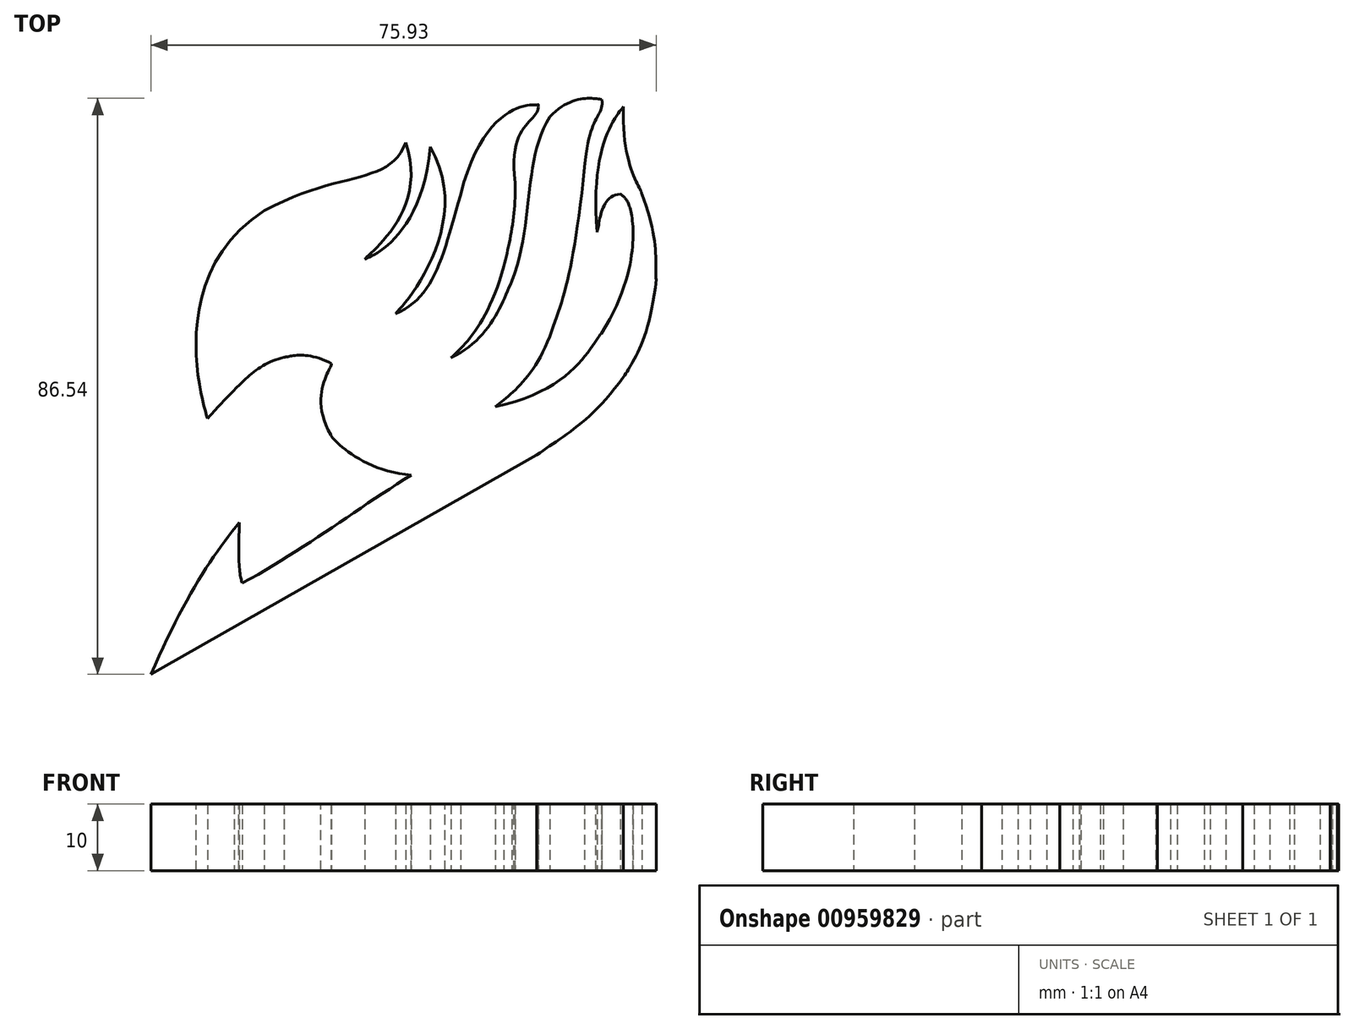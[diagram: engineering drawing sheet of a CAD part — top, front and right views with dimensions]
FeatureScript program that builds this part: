
annotation { "Feature Type Name" : "Feature", "Feature Type Description" : "" }
export const myFeature = defineFeature(function(context is Context, id is Id, definition is map)
    precondition{}
    {
        {
            var Q0;
            Q0=qCreatedBy(makeId("Top.planeOp"),FACE);
            var sketch = newSketch(context, id + "F0", { "sketchPlane" : qUnion([Q0])});
            skFitSpline(sketch, "E0", {"points": [v(8.52, 38.4) * mm, v(17.05, 69.64) * mm], "startDerivative": vector(-0.44, 1.4) * mm, "endDerivative": vector(47.56, 30.17) * mm});
            skFitSpline(sketch, "E1", {"points": [v(17.05, 69.64) * mm, v(38.3, 79.88) * mm], "startDerivative": vector(34.34, 18.82) * mm, "endDerivative": vector(7.6, 19.81) * mm});
            skFitSpline(sketch, "E2", {"points": [v(38.3, 79.88) * mm, v(32.13, 62.27) * mm], "startDerivative": vector(10.9, -31.7) * mm, "endDerivative": vector(0, -1.98) * mm});
            skFitSpline(sketch, "E3", {"points": [v(32.13, 62.27) * mm, v(41.98, 79.22) * mm], "startDerivative": vector(-2.8, 0) * mm, "endDerivative": vector(4.05, 45.39) * mm});
            skFitSpline(sketch, "E4", {"points": [v(41.98, 79.22) * mm, v(36.55, 54.12) * mm], "startDerivative": vector(22.19, -37.86) * mm, "endDerivative": vector(2.45, 4.02) * mm});
            skFitSpline(sketch, "E5", {"points": [v(36.55, 54.12) * mm, v(46.52, 72.02) * mm], "startDerivative": vector(17.84, 6.65) * mm, "endDerivative": vector(8.05, 28.34) * mm});
            skFitSpline(sketch, "E6", {"points": [v(46.52, 72.02) * mm, v(58.18, 85.6) * mm], "startDerivative": vector(12.25, 47.76) * mm, "endDerivative": vector(-2.45, 1.22) * mm});
            skFitSpline(sketch, "E7", {"points": [v(54.72, 73.88) * mm, v(53.05, 61.3) * mm], "startDerivative": vector(0.6, -12.92) * mm, "endDerivative": vector(-2.62, -10.5) * mm});
            skFitSpline(sketch, "E8", {"points": [v(53.05, 61.3) * mm, v(45.12, 47.59) * mm], "startDerivative": vector(-7.35, -26.07) * mm, "endDerivative": vector(-5.77, -5.25) * mm});
            skFitSpline(sketch, "E9", {"points": [v(58.18, 85.6) * mm, v(54.72, 73.88) * mm], "startDerivative": vector(1.4, -8.22) * mm, "endDerivative": vector(3.43, -28.54) * mm});
            skFitSpline(sketch, "E10", {"points": [v(45.12, 47.59) * mm, v(54.23, 59.06) * mm], "startDerivative": vector(17.22, 7.9) * mm, "endDerivative": vector(4.81, 10.79) * mm});
            skFitSpline(sketch, "E11", {"points": [v(54.23, 59.06) * mm, v(59.93, 83.77) * mm], "startDerivative": vector(10.5, 28.09) * mm, "endDerivative": vector(12.27, 20.32) * mm});
            skFitSpline(sketch, "E12", {"points": [v(59.93, 83.77) * mm, v(67.77, 86.36) * mm], "startDerivative": vector(10.3, 10.7) * mm, "endDerivative": vector(3.22, -0.37) * mm});
            skFitSpline(sketch, "E13", {"points": [v(67.77, 86.36) * mm, v(65.18, 76.23) * mm], "startDerivative": vector(0.9, -8.86) * mm, "endDerivative": vector(-2.02, -24.68) * mm});
            skFitSpline(sketch, "E14", {"points": [v(65.18, 76.23) * mm, v(59.93, 50.75) * mm], "startDerivative": vector(-5.05, -48.17) * mm, "endDerivative": vector(-6.38, -17.67) * mm});
            skFitSpline(sketch, "E15", {"points": [v(59.93, 50.75) * mm, v(51.78, 40.21) * mm], "startDerivative": vector(-7.56, -19.64) * mm, "endDerivative": vector(-6.48, -5.5) * mm});
            skFitSpline(sketch, "E16", {"points": [v(51.78, 40.21) * mm, v(67.68, 51.2) * mm], "startDerivative": vector(36.83, 7.57) * mm, "endDerivative": vector(3.36, 2.67) * mm});
            skFitSpline(sketch, "E17", {"points": [v(67.68, 51.2) * mm, v(72.46, 67.24) * mm], "startDerivative": vector(15.88, 24.97) * mm, "endDerivative": vector(0.02, 3.37) * mm});
            skFitSpline(sketch, "E18", {"points": [v(72.46, 67.24) * mm, v(70.56, 72.15) * mm], "startDerivative": vector(-1.07, 10.97) * mm, "endDerivative": vector(-2.7, 2) * mm});
            skFitSpline(sketch, "E19", {"points": [v(70.56, 72.15) * mm, v(67.03, 66.4) * mm], "startDerivative": vector(-9.55, -0.78) * mm, "endDerivative": vector(-1.4, -3.73) * mm});
            skFitSpline(sketch, "E20", {"points": [v(67.03, 66.4) * mm, v(71.02, 85.3) * mm], "startDerivative": vector(-3.14, 39.6) * mm, "endDerivative": vector(3.4, 4.39) * mm});
            skFitSpline(sketch, "E21", {"points": [v(71.02, 85.3) * mm, v(73.77, 72.15) * mm], "startDerivative": vector(-1.13, -26.95) * mm, "endDerivative": vector(0, -2.54) * mm});
            skFitSpline(sketch, "E22", {"points": [v(73.77, 72.15) * mm, v(75.93, 59.32) * mm], "startDerivative": vector(8.47, -21.25) * mm, "endDerivative": vector(0.63, -3.94) * mm});
            skFitSpline(sketch, "E23", {"points": [v(75.93, 59.32) * mm, v(71.02, 44.66) * mm], "startDerivative": vector(-2.9, -28.25) * mm, "endDerivative": vector(-3.42, -5.77) * mm});
            skFitSpline(sketch, "E24", {"points": [v(71.02, 44.66) * mm, v(58, 32.95) * mm], "startDerivative": vector(-15.68, -21.57) * mm, "endDerivative": vector(-10.6, -7.83) * mm});
            skFitSpline(sketch, "E25", {"points": [v(58, 32.95) * mm, v(0, 0) * mm], "startDerivative": vector(-58, -32.95) * mm, "endDerivative": vector(-58, -32.95) * mm});
            skFitSpline(sketch, "E26", {"points": [v(0, 0) * mm, v(13.29, 22.8) * mm], "startDerivative": vector(14.08, 32.72) * mm, "endDerivative": vector(12.44, 15.11) * mm});
            skFitSpline(sketch, "E27", {"points": [v(13.29, 22.8) * mm, v(13.75, 13.7) * mm], "startDerivative": vector(-0.58, -15.67) * mm, "endDerivative": vector(1.59, -3.1) * mm});
            skFitSpline(sketch, "E28", {"points": [v(13.75, 13.7) * mm, v(39.14, 29.94) * mm], "startDerivative": vector(27.51, 14.78) * mm, "endDerivative": vector(25.5, 15.76) * mm});
            skFitSpline(sketch, "E29", {"points": [v(39.14, 29.94) * mm, v(27.03, 35.96) * mm], "startDerivative": vector(-21.99, 1.48) * mm, "endDerivative": vector(-0.62, 1.94) * mm});
            skFitSpline(sketch, "E30", {"points": [v(27.03, 35.96) * mm, v(27.14, 46.66) * mm], "startDerivative": vector(-10.31, 17.52) * mm, "endDerivative": vector(0, 2.34) * mm});
            skFitSpline(sketch, "E31", {"points": [v(27.14, 46.66) * mm, v(20.03, 47.63) * mm], "startDerivative": vector(-11.37, 6.18) * mm, "endDerivative": vector(-2, -0.1) * mm});
            skFitSpline(sketch, "E32", {"points": [v(20.03, 47.63) * mm, v(12.5, 42.68) * mm], "startDerivative": vector(-10.24, -2.32) * mm, "endDerivative": vector(-4.92, -5.33) * mm});
            skFitSpline(sketch, "E33", {"points": [v(12.5, 42.68) * mm, v(8.52, 38.4) * mm], "startDerivative": vector(-3.93, -3.97) * mm, "endDerivative": vector(-2.97, -3.7) * mm});
            skSolve(sketch);
        }
        {
            var Q0;
            Q0 = qSketchRegion(id + "F0", true);
            extrude(context, id + "F1", {"entities" : qUnion([Q0]), "depth" : 10 * mm, "offsetDistance" : 25 * mm});
        }
    });
